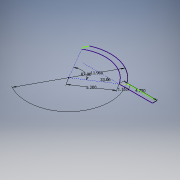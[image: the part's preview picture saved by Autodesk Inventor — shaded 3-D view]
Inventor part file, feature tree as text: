
AUTODESK INVENTOR PART (.ipt)
format: ipt  version: 2017 (Build 210142000, 142)  size: 94,208 bytes
history: native  units: in
note: dims shown in document units (in); Inventor stores cm internally (conversion verified against a paired STEP export)
features: sketch x1
ambient origin geometry x8: Origin, YZ Plane, XZ Plane, XY Plane, X Axis, Y Axis, Z Axis, Center Point
feature tree (1):
  sketch  "Sketch1"  dims[d1=5.2in d2=0.2272in d3=0.5978in d4=11.9in d5=1.152in d6=4.75in]
